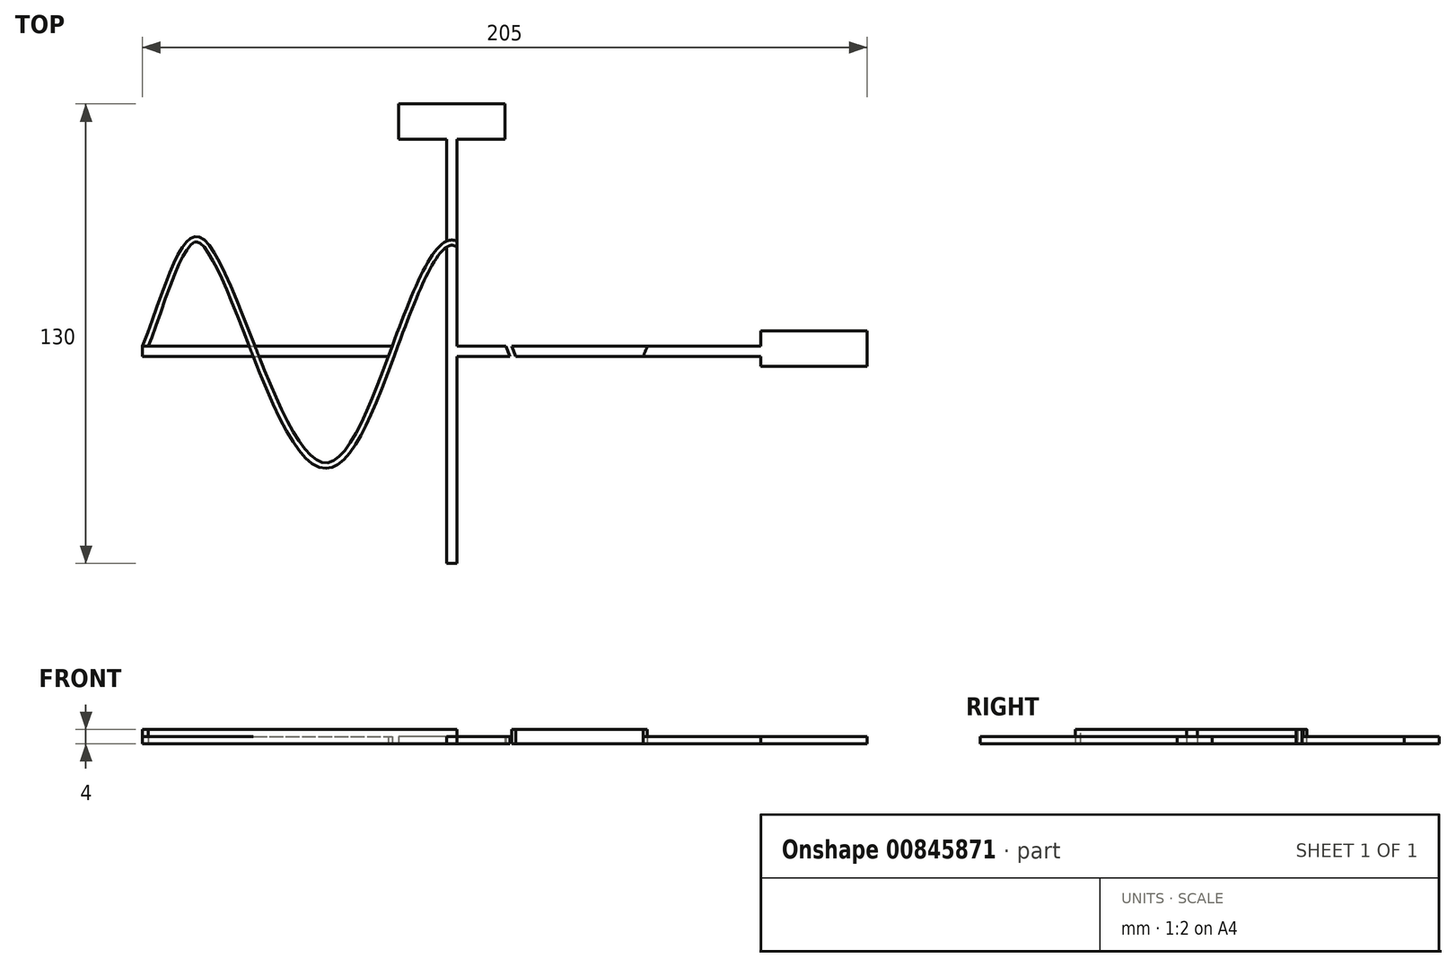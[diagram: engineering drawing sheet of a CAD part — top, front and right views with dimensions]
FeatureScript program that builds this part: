
annotation { "Feature Type Name" : "Feature", "Feature Type Description" : "" }
export const myFeature = defineFeature(function(context is Context, id is Id, definition is map)
    precondition{}
    {
        {
            var Q0;
            Q0=qCreatedBy(makeId("Top.planeOp"),FACE);
            var sketch = newSketch(context, id + "F0", { "sketchPlane" : qUnion([Q0])});
            skLineSegment(sketch, "E0.bottom", {"start": v(-87.5, 1.5) * mm, "end": v(87.5, 1.5) * mm});
            skLineSegment(sketch, "E0.top", {"start": v(-87.5, -1.5) * mm, "end": v(87.5, -1.5) * mm});
            skLineSegment(sketch, "E0.left", {"start": v(-87.5, 1.5) * mm, "end": v(-87.5, -1.5) * mm});
            skLineSegment(sketch, "E0.right", {"start": v(87.5, 1.5) * mm, "end": v(87.5, -1.5) * mm});
            skLineSegment(sketch, "E1.bottom", {"start": v(-1.5, 60) * mm, "end": v(1.5, 60) * mm});
            skLineSegment(sketch, "E1.top", {"start": v(-1.5, -60) * mm, "end": v(1.5, -60) * mm});
            skLineSegment(sketch, "E1.left", {"start": v(-1.5, 60) * mm, "end": v(-1.5, -60) * mm});
            skLineSegment(sketch, "E1.right", {"start": v(1.5, 60) * mm, "end": v(1.5, -60) * mm});
            skPoint(sketch, "E1.middle", {"position": v(0, 0) * mm});
            skLineSegment(sketch, "E2.bottom", {"start": v(15, 60) * mm, "end": v(-15, 60) * mm});
            skLineSegment(sketch, "E2.top", {"start": v(15, 70) * mm, "end": v(-15, 70) * mm});
            skLineSegment(sketch, "E2.left", {"start": v(15, 60) * mm, "end": v(15, 70) * mm});
            skLineSegment(sketch, "E2.right", {"start": v(-15, 60) * mm, "end": v(-15, 70) * mm});
            skPoint(sketch, "E2.middle", {"position": v(0, 65) * mm});
            skPoint(sketch, "E3", {"position": v(0, 60) * mm});
            skLineSegment(sketch, "E4.bottom", {"start": v(101, -4.26) * mm, "end": v(104, -4.26) * mm});
            skLineSegment(sketch, "E5.bottom", {"start": v(117.5, -4.26) * mm, "end": v(87.5, -4.26) * mm});
            skLineSegment(sketch, "E5.top", {"start": v(117.5, 5.74) * mm, "end": v(87.5, 5.74) * mm});
            skLineSegment(sketch, "E5.left", {"start": v(117.5, -4.26) * mm, "end": v(117.5, 5.74) * mm});
            skLineSegment(sketch, "E5.right", {"start": v(87.5, -4.26) * mm, "end": v(87.5, 5.74) * mm});
            skPoint(sketch, "E5.middle", {"position": v(102.5, 0.74) * mm});
            skPoint(sketch, "E6", {"position": v(102.5, -4.26) * mm});
            skPoint(sketch, "E7", {"position": v(87.5, 0) * mm});
            skPoint(sketch, "E8", {"position": v(0, 1.5) * mm});
            skLineSegment(sketch, "E9", {"start": v(-90, 31.5) * mm, "end": v(86.69, 31.5) * mm, "construction": true});
            skLineSegment(sketch, "E10", {"start": v(-87.09, -31.5) * mm, "end": v(87.56, -31.5) * mm, "construction": true});
            skPoint(sketch, "E11", {"position": v(-70, 31.5) * mm});
            skPoint(sketch, "E12", {"position": v(0, 31.5) * mm});
            skPoint(sketch, "E13", {"position": v(70, 31.5) * mm});
            skPoint(sketch, "E14", {"position": v(-35, -31.5) * mm});
            skPoint(sketch, "E15", {"position": v(35, -31.5) * mm});
            skFitSpline(sketch, "E16", {"points": [v(-87.5, 1.5) * mm, v(-70, 31.5) * mm, v(-35, -31.5) * mm, v(0, 31.5) * mm, v(35, -31.5) * mm, v(70, 31.5) * mm, v(87.5, 1.5) * mm], "startDerivative": vector(156.57, 404.06) * mm, "endDerivative": vector(107.76, -419.72) * mm});
            skFitSpline(sketch, "E17.0", {"points": [v(-86.1, 0.96) * mm, v(-85.28, 3.08) * mm, v(-83.71, 7.33) * mm, v(-81.53, 13.5) * mm, v(-79.47, 19.17) * mm, v(-77.82, 23.28) * mm, v(-76.53, 26.03) * mm, v(-75.59, 27.8) * mm, v(-74.66, 29.21) * mm, v(-73.8, 30.24) * mm, v(-73.16, 30.73) * mm, v(-72.75, 30.92) * mm, v(-72.5, 31) * mm, v(-72.28, 31.01) * mm, v(-72.04, 30.98) * mm, v(-71.76, 30.89) * mm, v(-71.4, 30.7) * mm, v(-70.98, 30.38) * mm, v(-70.34, 29.77) * mm, v(-69.43, 28.64) * mm, v(-68.25, 26.78) * mm, v(-67, 24.5) * mm, v(-65.7, 21.83) * mm, v(-63.9, 17.85) * mm, v(-61.57, 12.22) * mm, v(-58.65, 4.8) * mm, v(-55.64, -2.9) * mm, v(-52.55, -10.47) * mm, v(-49.39, -17.54) * mm, v(-46.71, -22.71) * mm, v(-44.53, -26.23) * mm, v(-42.87, -28.53) * mm, v(-41.16, -30.43) * mm, v(-39.37, -31.9) * mm, v(-37.76, -32.72) * mm, v(-36.36, -33.04) * mm, v(-35.29, -33.08) * mm, v(-34.21, -32.9) * mm, v(-33.2, -32.53) * mm, v(-32.23, -32) * mm, v(-31.02, -31.1) * mm, v(-29.6, -29.67) * mm, v(-27.97, -27.52) * mm, v(-26.4, -24.99) * mm, v(-24.86, -22.1) * mm, v(-23.33, -18.92) * mm, v(-21.33, -14.34) * mm, v(-18.85, -8.12) * mm, v(-15.9, -0.26) * mm, v(-13, 7.55) * mm, v(-10.6, 13.67) * mm, v(-8.7, 18.1) * mm, v(-7.28, 21.14) * mm, v(-5.87, 23.84) * mm, v(-4.49, 26.12) * mm, v(-3.15, 27.94) * mm, v(-2.1, 29) * mm, v(-1.34, 29.56) * mm, v(-0.83, 29.83) * mm, v(-0.38, 29.97) * mm, v(0, 30.01) * mm, v(0.39, 29.97) * mm, v(0.83, 29.83) * mm, v(1.35, 29.56) * mm, v(2.1, 29) * mm, v(3.16, 27.95) * mm, v(4.5, 26.14) * mm, v(5.9, 23.86) * mm, v(7.31, 21.17) * mm, v(8.74, 18.13) * mm, v(10.66, 13.7) * mm, v(13.07, 7.6) * mm, v(16, -0.22) * mm, v(18.95, -8.07) * mm, v(21.43, -14.3) * mm, v(23.44, -18.87) * mm, v(24.95, -22.06) * mm, v(26.49, -24.94) * mm, v(28.05, -27.48) * mm, v(29.65, -29.63) * mm, v(31.05, -31.07) * mm, v(32.25, -31.97) * mm, v(33.2, -32.51) * mm, v(34.2, -32.9) * mm, v(35.27, -33.08) * mm, v(36.33, -33.05) * mm, v(37.71, -32.74) * mm, v(39.3, -31.93) * mm, v(41.06, -30.46) * mm, v(42.72, -28.57) * mm, v(44.34, -26.29) * mm, v(45.93, -23.66) * mm, v(47.5, -20.73) * mm, v(49.58, -16.47) * mm, v(52.15, -10.6) * mm, v(55.19, -3.04) * mm, v(58.18, 4.64) * mm, v(61.1, 12.06) * mm, v(63.47, 17.7) * mm, v(65.31, 21.7) * mm, v(66.67, 24.37) * mm, v(67.98, 26.67) * mm, v(69.25, 28.55) * mm, v(70.23, 29.7) * mm, v(70.94, 30.35) * mm, v(71.43, 30.7) * mm, v(71.86, 30.92) * mm, v(72.25, 31.05) * mm, v(72.6, 31.1) * mm, v(72.92, 31.1) * mm, v(73.27, 31.02) * mm, v(73.78, 30.82) * mm, v(74.51, 30.35) * mm, v(75.49, 29.37) * mm, v(76.5, 28) * mm, v(77.54, 26.3) * mm, v(78.9, 23.6) * mm, v(80.58, 19.54) * mm, v(82.5, 13.87) * mm, v(84.34, 7.65) * mm, v(85.49, 3.3) * mm, v(86.05, 1.13) * mm]});
            skSolve(sketch);
        }
        {
            var Q0;
            Q0=makeQuery(id+"F0.imprint","IMPRINT",FACE,{"disambiguationData":[TD([[makeQuery(id+"F0.imprint","IMPRINT",EDGE,{"derivedFrom":sQuery(id+"F0.wireOp",EDGE,"E2.top")}),1.0]])]});
            var Q1;
            {var subQ0=sQuery(id+"F0.wireOp",EDGE,"E1.left");var subQ1=sQuery(id+"F0.wireOp",EDGE,"E0.bottom");var subQ2=makeQuery(id+"F0.imprint","INTERSECT",VERTEX,{"derivedFrom":[subQ1,subQ0]});Q1=makeQuery(id+"F0.imprint","IMPRINT",FACE,{"disambiguationData":[TD([[makeQuery(id+"F0.imprint","IMPRINT",EDGE,{"disambiguationData":[TD([[subQ2,-1.0]])],"derivedFrom":subQ1}),1.0]])]});}
            var Q2;
            {var subQ0=sQuery(id+"F0.wireOp",EDGE,"E5.right");var subQ1=sQuery(id+"F0.wireOp",EDGE,"E0.bottom");var subQ2=makeQuery(id+"F0.imprint","INTERSECT",VERTEX,{"derivedFrom":[subQ1,subQ0]});Q2=makeQuery(id+"F0.imprint","IMPRINT",FACE,{"disambiguationData":[TD([[makeQuery(id+"F0.imprint","IMPRINT",EDGE,{"disambiguationData":[TD([[subQ2,1.0]])],"derivedFrom":subQ1}),-1.0]])]});}
            var Q3;
            {var subQ0=sQuery(id+"F0.wireOp",EDGE,"E0.left");Q3=makeQuery(id+"F0.imprint","IMPRINT",FACE,{"disambiguationData":[TD([[makeQuery(id+"F0.imprint","IMPRINT",EDGE,{"derivedFrom":subQ0}),1.0]])]});}
            var Q4;
            {var subQ5=sQuery(id+"F0.wireOp",EDGE,"E5.top");Q4=makeQuery(id+"F0.imprint","IMPRINT",FACE,{"disambiguationData":[TD([[makeQuery(id+"F0.imprint","IMPRINT",EDGE,{"derivedFrom":subQ5}),1.0]])]});}
            var Q5;
            {var subQ5=sQuery(id+"F0.wireOp",EDGE,"E1.top");Q5=makeQuery(id+"F0.imprint","IMPRINT",FACE,{"disambiguationData":[TD([[makeQuery(id+"F0.imprint","IMPRINT",EDGE,{"derivedFrom":subQ5}),1.0]])]});}
            var Q6;
            {var subQ0=sQuery(id+"F0.wireOp",EDGE,"E1.left");var subQ1=sQuery(id+"F0.wireOp",EDGE,"E0.bottom");var subQ2=makeQuery(id+"F0.imprint","INTERSECT",VERTEX,{"derivedFrom":[subQ1,subQ0]});Q6=makeQuery(id+"F0.imprint","IMPRINT",FACE,{"disambiguationData":[TD([[makeQuery(id+"F0.imprint","IMPRINT",EDGE,{"disambiguationData":[TD([[subQ2,-1.0]])],"derivedFrom":subQ1}),-1.0]])]});}
            var Q7;
            {var subQ0=sQuery(id+"F0.wireOp",EDGE,"E16");var subQ1=sQuery(id+"F0.wireOp",EDGE,"E0.bottom");var subQ2=makeQuery(id+"F0.imprint","INTERSECT",VERTEX,{"disambiguationData":[OD(0.0)],"derivedFrom":[subQ1,subQ0]});Q7=makeQuery(id+"F0.imprint","IMPRINT",FACE,{"disambiguationData":[TD([[makeQuery(id+"F0.imprint","IMPRINT",EDGE,{"disambiguationData":[TD([[subQ2,-1.0]])],"derivedFrom":subQ1}),-1.0]])]});}
            var Q8;
            {var subQ0=sQuery(id+"F0.wireOp",EDGE,"E16");var subQ1=sQuery(id+"F0.wireOp",EDGE,"E0.bottom");var subQ2=makeQuery(id+"F0.imprint","INTERSECT",VERTEX,{"disambiguationData":[OD(2.0)],"derivedFrom":[subQ1,subQ0]});Q8=makeQuery(id+"F0.imprint","IMPRINT",FACE,{"disambiguationData":[TD([[makeQuery(id+"F0.imprint","IMPRINT",EDGE,{"disambiguationData":[TD([[subQ2,-1.0]])],"derivedFrom":subQ1}),-1.0]])]});}
            var Q9;
            {var subQ0=sQuery(id+"F0.wireOp",EDGE,"E2.bottom");var subQ1=sQuery(id+"F0.wireOp",EDGE,"E1.left");var subQ2=makeQuery(id+"F0.imprint","INTERSECT",VERTEX,{"derivedFrom":[subQ1,subQ0]});Q9=makeQuery(id+"F0.imprint","IMPRINT",FACE,{"disambiguationData":[TD([[makeQuery(id+"F0.imprint","IMPRINT",EDGE,{"disambiguationData":[TD([[subQ2,-1.0]])],"derivedFrom":subQ1}),1.0]])]});}
            var Q10;
            {var subQ0=sQuery(id+"F0.wireOp",EDGE,"E17.0");var subQ1=sQuery(id+"F0.wireOp",EDGE,"E0.bottom");var subQ2=makeQuery(id+"F0.imprint","INTERSECT",VERTEX,{"disambiguationData":[OD(3.0)],"derivedFrom":[subQ1,subQ0]});Q10=makeQuery(id+"F0.imprint","IMPRINT",FACE,{"disambiguationData":[TD([[makeQuery(id+"F0.imprint","IMPRINT",EDGE,{"disambiguationData":[TD([[subQ2,-1.0]])],"derivedFrom":subQ1}),-1.0]])]});}
            var Q11;
            {var subQ0=sQuery(id+"F0.wireOp",EDGE,"E1.right");var subQ1=sQuery(id+"F0.wireOp",EDGE,"E0.bottom");var subQ2=makeQuery(id+"F0.imprint","INTERSECT",VERTEX,{"derivedFrom":[subQ1,subQ0]});Q11=makeQuery(id+"F0.imprint","IMPRINT",FACE,{"disambiguationData":[TD([[makeQuery(id+"F0.imprint","IMPRINT",EDGE,{"disambiguationData":[TD([[subQ2,-1.0]])],"derivedFrom":subQ1}),-1.0]])]});}
            extrude(context, id + "F1", {"entities" : qUnion([Q0, Q1, Q2, Q3, Q4, Q5, Q6, Q7, Q8, Q9, Q10, Q11]), "depth" : 2 * mm, "offsetDistance" : 25 * mm});
        }
        {
            var Q0;
            {var subQ0=sQuery(id+"F0.wireOp",EDGE,"E16");var subQ1=sQuery(id+"F0.wireOp",EDGE,"E0.bottom");var subQ5=makeQuery(id+"F0.imprint","INTERSECT",VERTEX,{"disambiguationData":[OD(0.0)],"derivedFrom":[subQ1,subQ0]});Q0=makeQuery(id+"F0.imprint","IMPRINT",FACE,{"disambiguationData":[TD([[makeQuery(id+"F0.imprint","IMPRINT",EDGE,{"disambiguationData":[TD([[subQ5,1.0]])],"derivedFrom":subQ1}),1.0]])]});}
            var Q1;
            {var subQ0=sQuery(id+"F0.wireOp",EDGE,"E16");var subQ1=sQuery(id+"F0.wireOp",EDGE,"E0.bottom");var subQ2=makeQuery(id+"F0.imprint","INTERSECT",VERTEX,{"disambiguationData":[OD(0.0)],"derivedFrom":[subQ1,subQ0]});Q1=makeQuery(id+"F0.imprint","IMPRINT",FACE,{"disambiguationData":[TD([[makeQuery(id+"F0.imprint","IMPRINT",EDGE,{"disambiguationData":[TD([[subQ2,1.0]])],"derivedFrom":subQ1}),-1.0]])]});}
            var Q2;
            {var subQ0=sQuery(id+"F0.wireOp",EDGE,"E17.0");var subQ1=sQuery(id+"F0.wireOp",EDGE,"E0.top");var subQ2=makeQuery(id+"F0.imprint","INTERSECT",VERTEX,{"disambiguationData":[OD(0.0)],"derivedFrom":[subQ1,subQ0]});Q2=makeQuery(id+"F0.imprint","IMPRINT",FACE,{"disambiguationData":[TD([[makeQuery(id+"F0.imprint","IMPRINT",EDGE,{"disambiguationData":[TD([[subQ2,-1.0]])],"derivedFrom":subQ1}),-1.0]])]});}
            var Q3;
            {var subQ0=sQuery(id+"F0.wireOp",EDGE,"E16");var subQ1=sQuery(id+"F0.wireOp",EDGE,"E0.bottom");var subQ2=makeQuery(id+"F0.imprint","INTERSECT",VERTEX,{"disambiguationData":[OD(1.0)],"derivedFrom":[subQ1,subQ0]});Q3=makeQuery(id+"F0.imprint","IMPRINT",FACE,{"disambiguationData":[TD([[makeQuery(id+"F0.imprint","IMPRINT",EDGE,{"disambiguationData":[TD([[subQ2,-1.0]])],"derivedFrom":subQ1}),-1.0]])]});}
            var Q4;
            {var subQ0=sQuery(id+"F0.wireOp",EDGE,"E16");var subQ1=sQuery(id+"F0.wireOp",EDGE,"E0.bottom");var subQ2=makeQuery(id+"F0.imprint","INTERSECT",VERTEX,{"disambiguationData":[OD(1.0)],"derivedFrom":[subQ1,subQ0]});Q4=makeQuery(id+"F0.imprint","IMPRINT",FACE,{"disambiguationData":[TD([[makeQuery(id+"F0.imprint","IMPRINT",EDGE,{"disambiguationData":[TD([[subQ2,-1.0]])],"derivedFrom":subQ1}),1.0]])]});}
            var Q5;
            {var subQ0=sQuery(id+"F0.wireOp",EDGE,"E16");var subQ1=sQuery(id+"F0.wireOp",EDGE,"E1.left");var subQ2=makeQuery(id+"F0.imprint","INTERSECT",VERTEX,{"derivedFrom":[subQ1,subQ0]});Q5=makeQuery(id+"F0.imprint","IMPRINT",FACE,{"disambiguationData":[TD([[makeQuery(id+"F0.imprint","IMPRINT",EDGE,{"disambiguationData":[TD([[subQ2,-1.0]])],"derivedFrom":subQ1}),1.0]])]});}
            var Q6;
            {var subQ0=sQuery(id+"F0.wireOp",EDGE,"E16");var subQ1=sQuery(id+"F0.wireOp",EDGE,"E0.bottom");var subQ2=makeQuery(id+"F0.imprint","INTERSECT",VERTEX,{"disambiguationData":[OD(2.0)],"derivedFrom":[subQ1,subQ0]});Q6=makeQuery(id+"F0.imprint","IMPRINT",FACE,{"disambiguationData":[TD([[makeQuery(id+"F0.imprint","IMPRINT",EDGE,{"disambiguationData":[TD([[subQ2,1.0]])],"derivedFrom":subQ1}),1.0]])]});}
            var Q7;
            {var subQ0=sQuery(id+"F0.wireOp",EDGE,"E16");var subQ1=sQuery(id+"F0.wireOp",EDGE,"E0.bottom");var subQ2=makeQuery(id+"F0.imprint","INTERSECT",VERTEX,{"disambiguationData":[OD(2.0)],"derivedFrom":[subQ1,subQ0]});Q7=makeQuery(id+"F0.imprint","IMPRINT",FACE,{"disambiguationData":[TD([[makeQuery(id+"F0.imprint","IMPRINT",EDGE,{"disambiguationData":[TD([[subQ2,1.0]])],"derivedFrom":subQ1}),-1.0]])]});}
            var Q8;
            {var subQ0=sQuery(id+"F0.wireOp",EDGE,"E17.0");var subQ1=sQuery(id+"F0.wireOp",EDGE,"E0.top");var subQ2=makeQuery(id+"F0.imprint","INTERSECT",VERTEX,{"disambiguationData":[OD(2.0)],"derivedFrom":[subQ1,subQ0]});Q8=makeQuery(id+"F0.imprint","IMPRINT",FACE,{"disambiguationData":[TD([[makeQuery(id+"F0.imprint","IMPRINT",EDGE,{"disambiguationData":[TD([[subQ2,-1.0]])],"derivedFrom":subQ1}),-1.0]])]});}
            var Q9;
            {var subQ0=sQuery(id+"F0.wireOp",EDGE,"E16");var subQ1=sQuery(id+"F0.wireOp",EDGE,"E0.bottom");var subQ2=makeQuery(id+"F0.imprint","INTERSECT",VERTEX,{"disambiguationData":[OD(3.0)],"derivedFrom":[subQ1,subQ0]});Q9=makeQuery(id+"F0.imprint","IMPRINT",FACE,{"disambiguationData":[TD([[makeQuery(id+"F0.imprint","IMPRINT",EDGE,{"disambiguationData":[TD([[subQ2,-1.0]])],"derivedFrom":subQ1}),-1.0]])]});}
            var Q10;
            {var subQ0=sQuery(id+"F0.wireOp",EDGE,"E16");var subQ1=sQuery(id+"F0.wireOp",EDGE,"E0.bottom");var subQ2=makeQuery(id+"F0.imprint","INTERSECT",VERTEX,{"disambiguationData":[OD(3.0)],"derivedFrom":[subQ1,subQ0]});Q10=makeQuery(id+"F0.imprint","IMPRINT",FACE,{"disambiguationData":[TD([[makeQuery(id+"F0.imprint","IMPRINT",EDGE,{"disambiguationData":[TD([[subQ2,-1.0]])],"derivedFrom":subQ1}),1.0]])]});}
            extrude(context, id + "F2", {"entities" : qUnion([Q0, Q1, Q2, Q3, Q4, Q5, Q6, Q7, Q8, Q9, Q10]), "depth" : 4 * mm, "offsetDistance" : 25 * mm});
        }
    });
